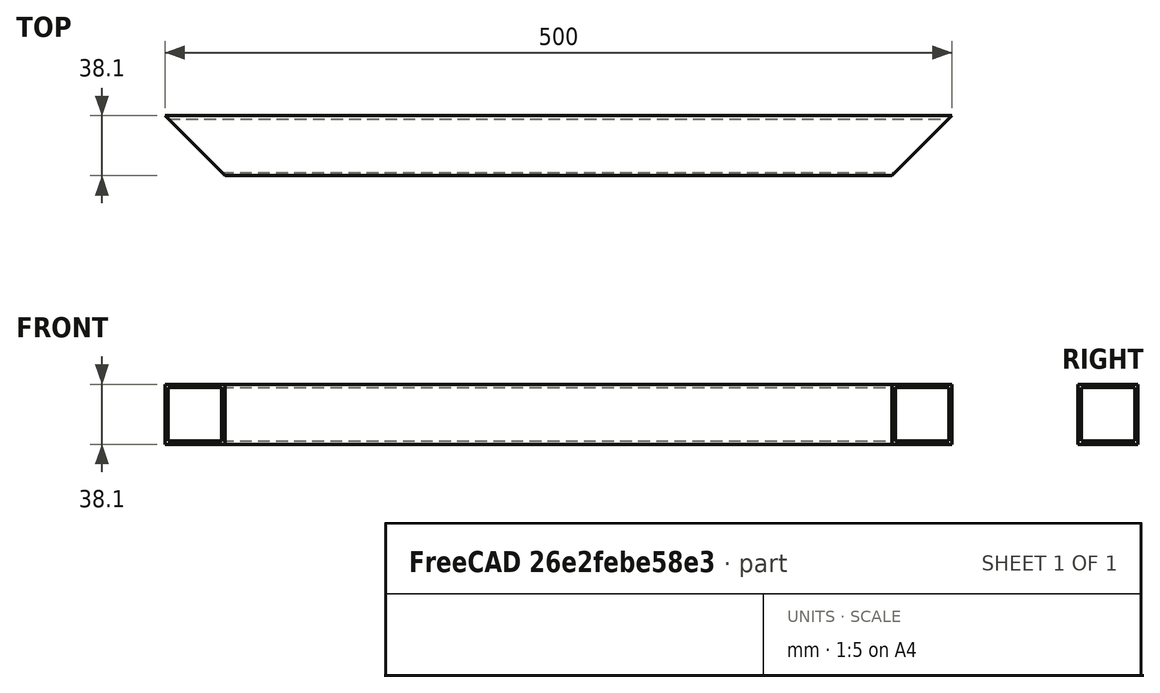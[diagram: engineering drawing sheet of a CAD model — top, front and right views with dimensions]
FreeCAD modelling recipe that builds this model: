
FCSTD DOCUMENT  (FreeCAD 0.18.4R)
Label: sp_ptc1ymedia(cal14)(50cm)(cut45)
License: All rights reserved
LicenseURL: http://en.wikipedia.org/wiki/All_rights_reserved
objects: Part::Cut×3, Part::Extrusion×2
note: 5 computed .brp shape members not serialized (recipe doc carries the construction recipe); baked Part::Feature solids carry a one-line shape summary decoded from their .brp

FEATURE [Part::Cut] Cut  label="sp_ptc1ymedia(cal14)(300cm)(cut90)"
FEATURE [Part::Extrusion] Extrude001  label="cortador45Izq"
  Dir = (0,0,1)
  DirMode = 2
  FaceMakerClass = Part::FaceMakerBullseye
  LengthFwd = 100
  LengthRev = 0
  Placement = pos=(38.1,0,0) rot=(0,0,1;0rad)
  Solid = true
  Symmetric = false
FEATURE [Part::Cut] Cut001
  Base = -> Cut
  Tool = -> Extrude001
FEATURE [Part::Extrusion] Extrude  label="cortador45Der"
  Dir = (0,0,1)
  DirMode = 2
  FaceMakerClass = Part::FaceMakerBullseye
  LengthFwd = 100
  LengthRev = 0
  Placement = pos=(461.9,0,0) rot=(0,0,1;0rad)
  Solid = true
  Symmetric = false
FEATURE [Part::Cut] Cut002
  Base = -> Cut001
  Tool = -> Extrude
